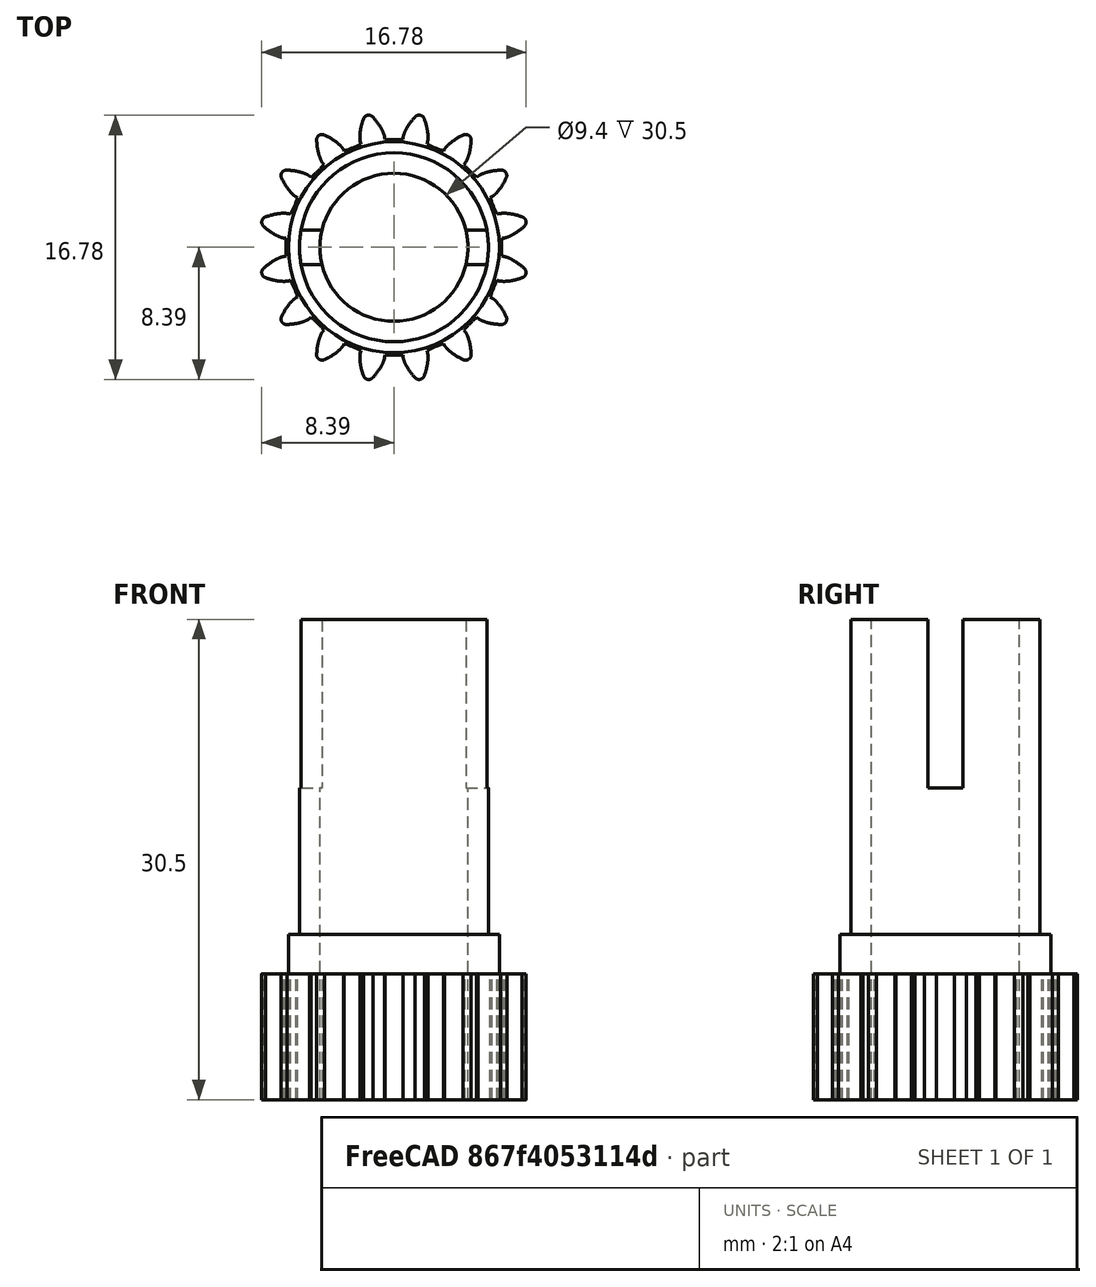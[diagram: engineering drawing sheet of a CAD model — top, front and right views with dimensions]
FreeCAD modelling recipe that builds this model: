
FCSTD DOCUMENT  (FreeCAD 0.17R13522 (Git))
Label: v5_bastago_con_engranaje
License: CreativeCommons Attribution-ShareAlike
LicenseURL: http://creativecommons.org/licenses/by-sa/4.0/
objects: Part::Cut×2, Part::Box×1, Part::Feature×1, Part::Cylinder×1
note: 5 computed .brp shape members not serialized (recipe doc carries the construction recipe); baked Part::Feature solids carry a one-line shape summary decoded from their .brp

FEATURE [Part::Box] Box  label="hueco aletas"
  AttacherType = Attacher::AttachEngine3D
  Height = 10.7
  Length = 16
  Placement = pos=(-8,-1.1,19.8) rot=(0,0,1;0rad)
  Width = 2.2
FEATURE [Part::Feature] Fusion003001  label="engranaje"
  shape: bbox 16.79 x 16.79 x 30.5 mm, 138 faces (baked)
FEATURE [Part::Cut] Cut  label="engranaje con calces"
  Base = -> Fusion003001
  Refine = true
  Tool = -> Box
FEATURE [Part::Cylinder] Cylinder
  Angle = 360
  AttacherType = Attacher::AttachEngine3D
  Height = 45
  Placement = pos=(0,0,-8) rot=(0,0,1;0rad)
  Radius = 4.7
FEATURE [Part::Cut] Cut001  label="engranaje001"
  Base = -> Cut
  Refine = true
  Tool = -> Cylinder
